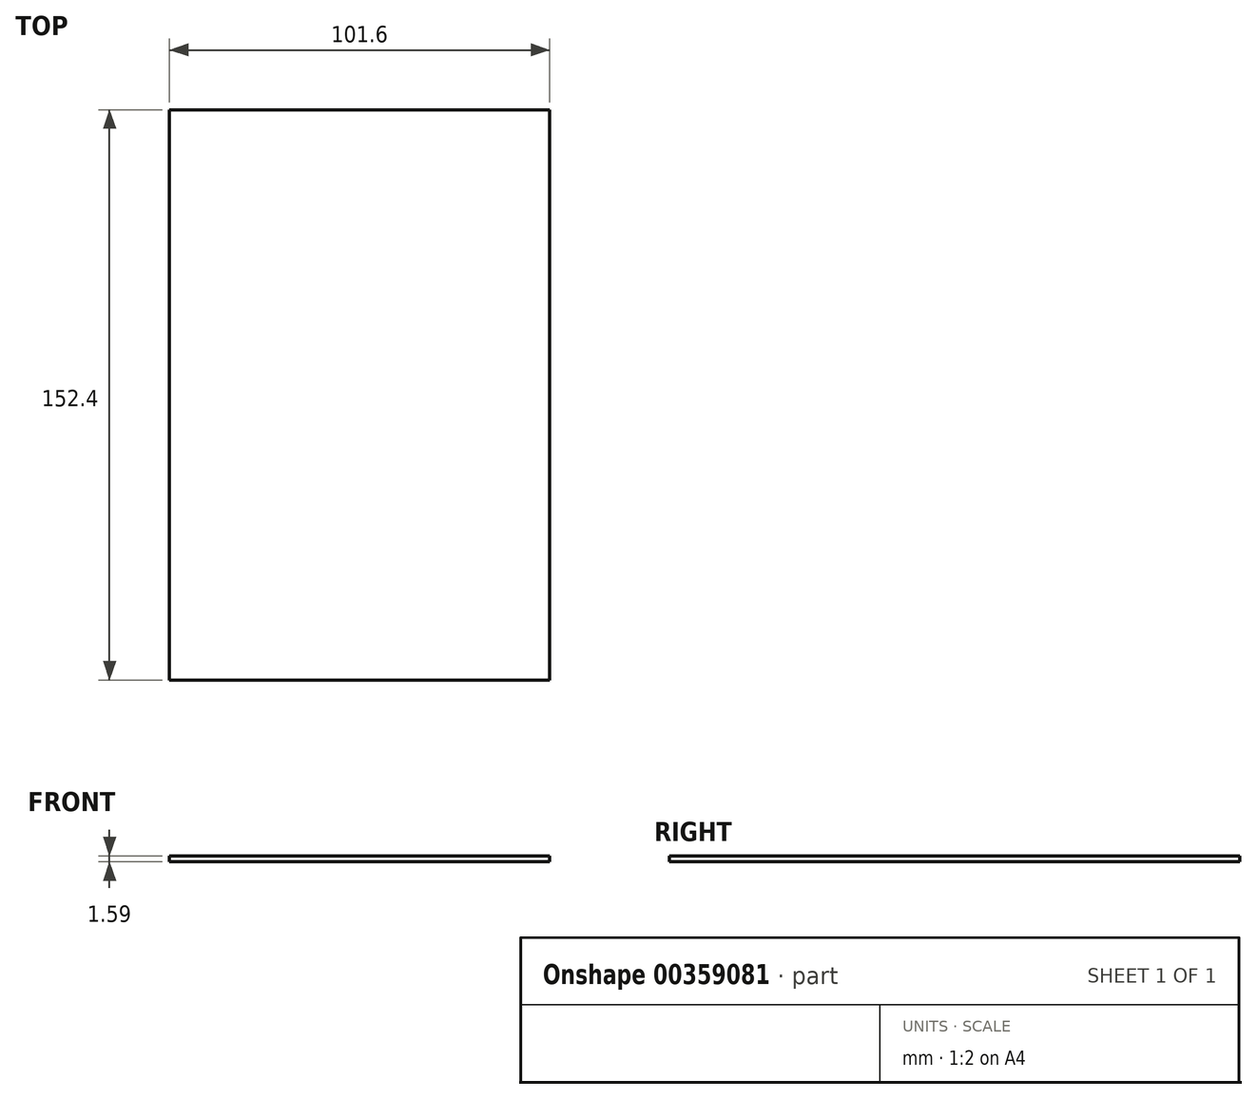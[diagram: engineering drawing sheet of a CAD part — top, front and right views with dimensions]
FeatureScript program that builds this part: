
annotation { "Feature Type Name" : "Feature", "Feature Type Description" : "" }
export const myFeature = defineFeature(function(context is Context, id is Id, definition is map)
    precondition{}
    {
        {
            var Q0;
            Q0=qCreatedBy(makeId("Top.planeOp"),FACE);
            var sketch = newSketch(context, id + "F0", { "sketchPlane" : qUnion([Q0])});
            skLineSegment(sketch, "E0.bottom", {"start": v(-44.39, 109.53) * mm, "end": v(57.21, 109.53) * mm});
            skLineSegment(sketch, "E0.top", {"start": v(-44.39, -42.87) * mm, "end": v(57.21, -42.87) * mm});
            skLineSegment(sketch, "E0.left", {"start": v(-44.39, 109.53) * mm, "end": v(-44.39, -42.87) * mm});
            skLineSegment(sketch, "E0.right", {"start": v(57.21, 109.53) * mm, "end": v(57.21, -42.87) * mm});
            skSolve(sketch);
        }
        {
            var Q0;
            Q0=makeQuery(id+"F0.imprint","IMPRINT",FACE,{"disambiguationData":[TD([[makeQuery(id+"F0.imprint","IMPRINT",EDGE,{"derivedFrom":sQuery(id+"F0.wireOp",EDGE,"E0.bottom")}),-1.0]])]});
            extrude(context, id + "F1", {"entities" : qUnion([Q0]), "depth" : 1.59 * mm});
        }
    });
